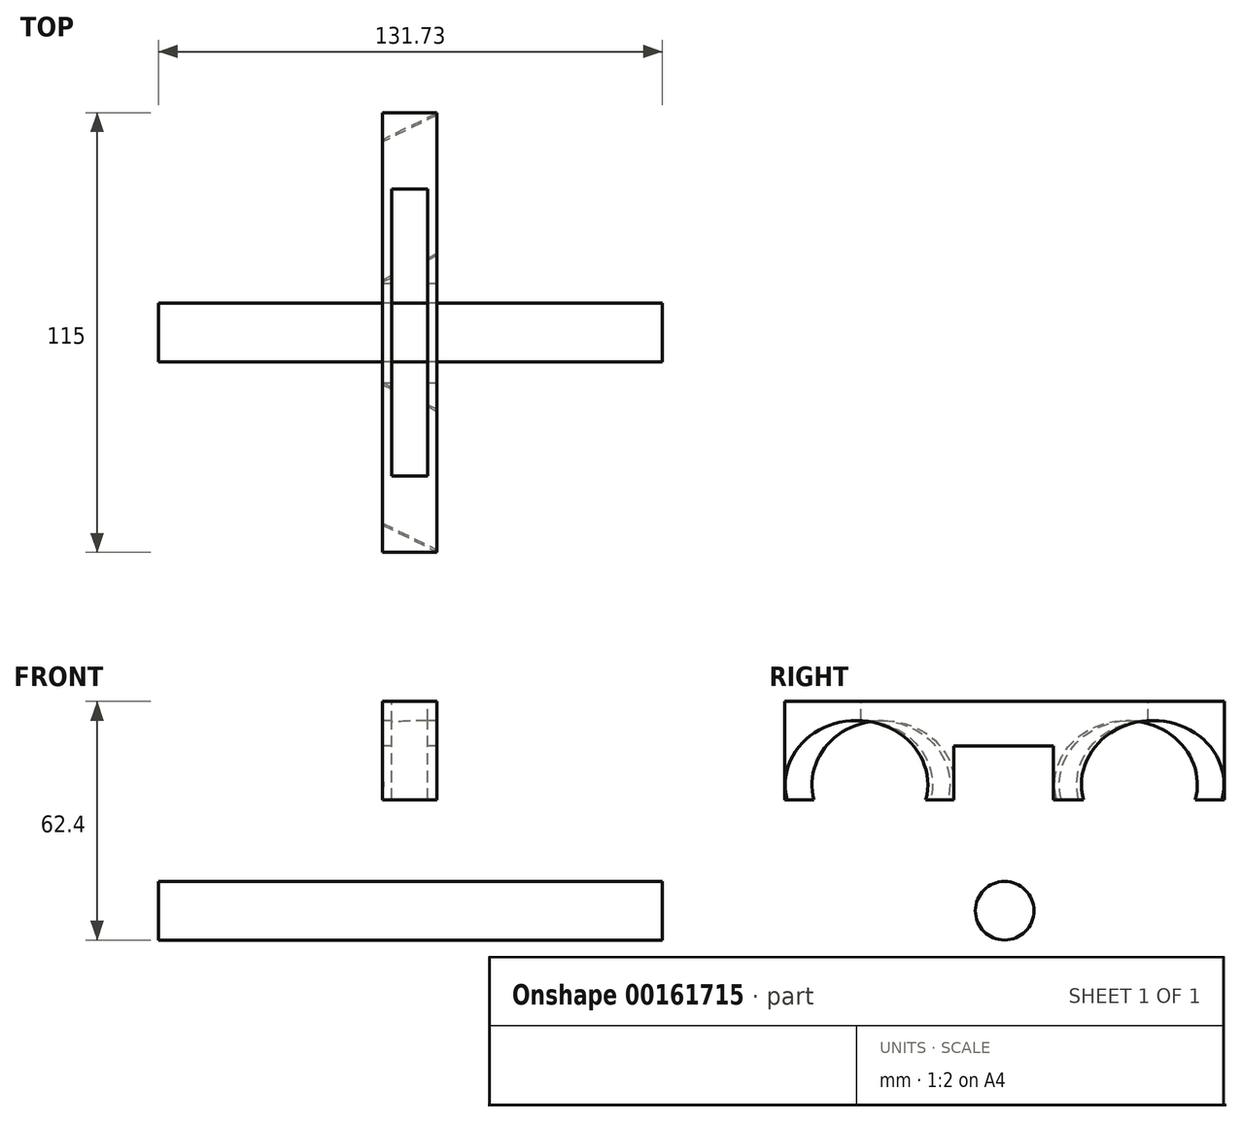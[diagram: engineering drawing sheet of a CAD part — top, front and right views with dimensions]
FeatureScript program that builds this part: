
annotation { "Feature Type Name" : "Feature", "Feature Type Description" : "" }
export const myFeature = defineFeature(function(context is Context, id is Id, definition is map)
    precondition{}
    {
        {
            var Q0;
            Q0=qCreatedBy(makeId("Top.planeOp"),FACE);
            var sketch = newSketch(context, id + "F0", { "sketchPlane" : qUnion([Q0])});
            skLineSegment(sketch, "E0", {"start": v(-126.96, 0) * mm, "end": v(6, 65) * mm});
            skLineSegment(sketch, "E1", {"start": v(6, 65) * mm, "end": v(6, -65) * mm});
            skLineSegment(sketch, "E2", {"start": v(6, -65) * mm, "end": v(-126.96, 0) * mm});
            skLineSegment(sketch, "E3", {"start": v(-126.96, 0) * mm, "end": v(-134.31, 15.05) * mm});
            skLineSegment(sketch, "E4", {"start": v(-134.31, 15.05) * mm, "end": v(-1.35, 80.05) * mm});
            skLineSegment(sketch, "E5", {"start": v(-1.35, 80.05) * mm, "end": v(6, 65) * mm});
            skLineSegment(sketch, "E6", {"start": v(-126.96, 0) * mm, "end": v(-134.31, -15.05) * mm});
            skLineSegment(sketch, "E7", {"start": v(-134.31, -15.05) * mm, "end": v(-1.35, -80.05) * mm});
            skLineSegment(sketch, "E8", {"start": v(-1.35, -80.05) * mm, "end": v(6, -65) * mm});
            skLineSegment(sketch, "E9", {"start": v(-50.25, 37.5) * mm, "end": v(-50.25, -37.5) * mm});
            skLineSegment(sketch, "E10", {"start": v(-134.31, 15.05) * mm, "end": v(-134.31, -15.05) * mm});
            skLineSegment(sketch, "E11", {"start": v(-126.96, 0) * mm, "end": v(0, 0) * mm, "construction": true});
            skSolve(sketch);
        }
        {
            var Q0;
            Q0=makeQuery(id+"F0.imprint","IMPRINT",FACE,{"disambiguationData":[TD([[makeQuery(id+"F0.imprint","IMPRINT",EDGE,{"derivedFrom":sQuery(id+"F0.wireOp",EDGE,"E0")}),1.0]])]});
            var Q1;
            Q1=sQuery(id+"F0.wireOp",EDGE,"E0");
            revolve(context, id + "F1", {"entities" : qUnion([Q0]), "axis" : qUnion([Q1]), "revolveType" : RevolveType.FULL});
        }
        {
            var Q0;
            Q0=makeQuery(id+"F0.imprint","IMPRINT",FACE,{"disambiguationData":[TD([[makeQuery(id+"F0.imprint","IMPRINT",EDGE,{"derivedFrom":sQuery(id+"F0.wireOp",EDGE,"E2")}),1.0]])]});
            var Q1;
            Q1=sQuery(id+"F0.wireOp",EDGE,"E2");
            revolve(context, id + "F2", {"operationType" : NewBodyOperationType.ADD, "entities" : qUnion([Q0]), "axis" : qUnion([Q1]), "revolveType" : RevolveType.FULL});
        }
        {
            var Q0;
            Q0=makeQuery(id+"F0.imprint","IMPRINT",FACE,{"disambiguationData":[TD([[makeQuery(id+"F0.imprint","IMPRINT",EDGE,{"derivedFrom":sQuery(id+"F0.wireOp",EDGE,"E3")}),1.0]])]});
            extrude(context, id + "F3", {"entities" : qUnion([Q0]), "operationType" : NewBodyOperationType.ADD, "endBound" : BoundingType.SYMMETRIC, "depth" : 33.5 * mm});
        }
        {
            var Q0;
            Q0=makeQuery(id+"F3.opExtrude","CAP_FACE",FACE,{"disambiguationData":[OSD([sQuery(id+"F0.wireOp",EDGE,"E3"),sQuery(id+"F0.wireOp",EDGE,"E6"),sQuery(id+"F0.wireOp",EDGE,"E10")])],"isStart":false});
            var sketch = newSketch(context, id + "F4", { "sketchPlane" : qUnion([Q0])});
            skLineSegment(sketch, "E12.0", {"start": v(-50.25, 37.5) * mm, "end": v(-50.25, -37.5) * mm});
            skLineSegment(sketch, "E13.0", {"start": v(-59.55, 37.5) * mm, "end": v(-59.55, -37.5) * mm});
            skLineSegment(sketch, "E14", {"start": v(-59.55, 37.5) * mm, "end": v(-50.25, 37.5) * mm});
            skLineSegment(sketch, "E15", {"start": v(-50.25, -37.5) * mm, "end": v(-59.55, -37.5) * mm});
            skLineSegment(sketch, "E16.bottom", {"start": v(-62.05, 57.5) * mm, "end": v(-47.75, 57.5) * mm});
            skLineSegment(sketch, "E16.top", {"start": v(-62.05, -57.5) * mm, "end": v(-47.75, -57.5) * mm});
            skLineSegment(sketch, "E16.left", {"start": v(-62.05, 57.5) * mm, "end": v(-62.05, -57.5) * mm});
            skLineSegment(sketch, "E16.right", {"start": v(-47.75, 57.5) * mm, "end": v(-47.75, -57.5) * mm});
            skSolve(sketch);
        }
        {
            var Q0;
            Q0=makeQuery(id+"F4.imprint","IMPRINT",FACE,{"disambiguationData":[TD([[makeQuery(id+"F4.imprint","IMPRINT",EDGE,{"derivedFrom":sQuery(id+"F4.wireOp",EDGE,"E12.0")}),1.0]])]});
            extrude(context, id + "F5", {"entities" : qUnion([Q0]), "oppositeDirection" : true, "depth" : (33.5 / 2 + 4) * mm});
        }
        {
            var Q0;
            Q0=makeQuery(id+"F4.imprint","IMPRINT",FACE,{"disambiguationData":[TD([[makeQuery(id+"F4.imprint","IMPRINT",EDGE,{"derivedFrom":sQuery(id+"F4.wireOp",EDGE,"E12.0")}),1.0]])]});
            extrude(context, id + "F6", {"entities" : qUnion([Q0]), "operationType" : NewBodyOperationType.ADD, "depth" : 5 * mm});
        }
        {
            var Q0;
            {var subQ0=sQuery(id+"F4.wireOp",EDGE,"E16.left");Q0=makeQuery(id+"F6.boolean.opBoolean","MERGE",FACE,{"derivedFrom":[makeQuery(id+"F5.opExtrude","SWEPT_FACE",FACE,{"disambiguationData":[OSD([subQ0])]}),makeQuery(id+"F6.opExtrude","SWEPT_FACE",FACE,{"disambiguationData":[OSD([subQ0])]})]});}
            var sketch = newSketch(context, id + "F7", { "sketchPlane" : qUnion([Q0])});
            skLineSegment(sketch, "E17.0", {"start": v(-57.5, -4) * mm, "end": v(57.5, -4) * mm});
            skLineSegment(sketch, "E18", {"start": v(-29.91, -16.75) * mm, "end": v(-94.91, -16.75) * mm});
            skLineSegment(sketch, "E19", {"start": v(-12.78, -4) * mm, "end": v(-12.78, 18.75) * mm});
            skLineSegment(sketch, "E20", {"start": v(13.27, -4) * mm, "end": v(13.27, 21.75) * mm});
            skLineSegment(sketch, "E21", {"start": v(-12.78, 10.15) * mm, "end": v(13.27, 10.15) * mm});
            skLineSegment(sketch, "E22", {"start": v(-12.78, 10.15) * mm, "end": v(-16.56, -4) * mm});
            skSolve(sketch);
        }
        {
            var Q0;
            {var subQ5=sQuery(id+"F7.wireOp",EDGE,"E21");Q0=makeQuery(id+"F7.imprint","IMPRINT",FACE,{"disambiguationData":[TD([[makeQuery(id+"F7.imprint","IMPRINT",EDGE,{"derivedFrom":subQ5}),-1.0]])]});}
            extrude(context, id + "F8", {"entities" : qUnion([Q0]), "operationType" : NewBodyOperationType.REMOVE, "oppositeDirection" : true, "depth" : 25 * mm});
        }
        {
            var Q0;
            Q0=qCreatedBy(makeId("Front.planeOp"),FACE);
            var sketch = newSketch(context, id + "F9", { "sketchPlane" : qUnion([Q0])});
            skLineSegment(sketch, "E23", {"start": v(-120.62, -33) * mm, "end": v(11.11, -33) * mm});
            skLineSegment(sketch, "E24", {"start": v(-120.62, -25.35) * mm, "end": v(11.11, -25.35) * mm});
            skLineSegment(sketch, "E25", {"start": v(11.11, -25.35) * mm, "end": v(11.11, -33) * mm});
            skLineSegment(sketch, "E26", {"start": v(-120.62, -25.35) * mm, "end": v(-120.62, -33) * mm});
            skSolve(sketch);
        }
        {
            var Q0;
            Q0=makeQuery(id+"F9.imprint","IMPRINT",FACE,{"disambiguationData":[TD([[makeQuery(id+"F9.imprint","IMPRINT",EDGE,{"derivedFrom":sQuery(id+"F9.wireOp",EDGE,"E23")}),1.0]])]});
            var Q1;
            Q1=sQuery(id+"F9.wireOp",EDGE,"E23");
            revolve(context, id + "F10", {"entities" : qUnion([Q0]), "axis" : qUnion([Q1]), "revolveType" : RevolveType.FULL});
        }
        {
            var Q0;
            Q0=makeQuery(id+"F1.opRevolve","SWEPT_BODY",BODY,{"disambiguationData":[OSD([sQuery(id+"F0.wireOp",EDGE,"E0"),sQuery(id+"F0.wireOp",EDGE,"E3"),sQuery(id+"F0.wireOp",EDGE,"E4"),sQuery(id+"F0.wireOp",EDGE,"E5")])]});
            var Q1;
            Q1=makeQuery(id+"F5.opExtrude","SWEPT_BODY",BODY,{"disambiguationData":[OSD([sQuery(id+"F4.wireOp",EDGE,"E12.0"),sQuery(id+"F4.wireOp",EDGE,"E13.0"),sQuery(id+"F4.wireOp",EDGE,"E14"),sQuery(id+"F4.wireOp",EDGE,"E15"),sQuery(id+"F4.wireOp",EDGE,"E16.bottom"),sQuery(id+"F4.wireOp",EDGE,"E16.top"),sQuery(id+"F4.wireOp",EDGE,"E16.left"),sQuery(id+"F4.wireOp",EDGE,"E16.right")])]});
            booleanBodies(context, id + "F11", {"operationType" : BooleanOperationType.SUBTRACTION, "tools" : qUnion([Q0]), "targets" : qUnion([Q1])});
        }
    });
